# Revit family: 3098169 Lighting Fixture_Sylvania_Insaver LED II 150 LO_Surface Mounted
name_source: partatom
category: Lighting Fixtures
revit_build: Autodesk Revit 2017 (Build: 20190507_1515(x64)
units: mm (PartAtom-declared; Revit-internal decimal feet)

## family parameters
Cut with Voids When Loaded = No
Host = Face
Light Source = Yes
OmniClass Number = 23.80.70.11.17
OmniClass Title = Specialized Lighting by Location or Use
Part Type = Normal
Room Calculation Point = No
Round Connector Dimension = Use Diameter
Shared = No

## types (1)
- Insaver LED II 150 Low Output NW EB Surface Mounted
    Accessory Diameter = 169 mm  [stored 0.554462 ft]
    Accessory Material = Plastic_Sylvania_Insaver LED II_White
    Accessory Radius = 84.5 mm  [stored 0.277231 ft]
    Apparent Load = 17 VA
    Assembly Code = D5020200
    Beam Angle = 76°
    Body Material = Plastic_Sylvania_Insaver LED II_White
    CRI ( Ra ) = 80
    Catalog Number = 3098169 Insaver LED II 150 Low Output NW EB Surface Mounted
    Color Filter = 16777215
    Colour consistency (SDCM) = 3 step
    Default Elevation = 0 mm  [stored 0 ft]
    Description = Circular LED downlight with up to 114lm/W efficacy and 2,400 luminaire lumen output. Innovative easy installation system allows for a rapid, single point installation. For 150mm cut outs. IP44 or UGR<19 compliant with additional accessories. 3 hour emergency and surface mounted versions available. Plus3 version includes Wieland GST connector.
    Diameter = 188 mm  [stored 0.616798 ft]
    Diffuser Diameter = 133 mm
    Diffuser Material = Glass_Sylvania_Insaver LED II_4000K
    Dimming Lamp Color Temperature Shift = <None>
    Distribution type = Direct - symmetrical
    Drive Current = 700mA
    Emit Shape Visible in Rendering = No
    Emit from Circle Diameter = 133 mm
    Energy Class = A++,A+,A
    Glare Control = UGR <19 (using accessory)
    Height = 208 mm
    IP Rating = IP23 (44 with accessory)
    LOR = 100%
    Lamp Comments = Integrated LED
    Life = 50 000 h
    Manufacturer = Feilo Sylvania
    Model = Insaver LED II 150 Low Output NW EB Surface Mounted
    Photometric Web File = 3098169_InsaverLEDII150LowOutputNWEBSurfaceMounted-202069.ies
    Product Family = INSAVER LED II 150 Surface Mounted
    Product Page URL = http://www.sylvania-lighting.com
    Radius = 94 mm  [stored 0.308399 ft]
    Reflector Material = Metal_Sylvania_Insaver LED II_Polished
    Ta Rating = 0°C to 55°C
    Tilt Angle = -90°
    URL = http://www.sylvania-lighting.com
    Voltage = 230 V
    Voltage Comments = UNV (Universal Voltage; 220-240 Volt)
    Weight = 0 kg

note: [stored X ft] marks values corroborated as IEEE doubles in the binary element streams (Revit-internal decimal feet)

## geometry (parser evidence)
native form markers: Blend x6, Sweep x3
no freeform markers — native parametric forms only
